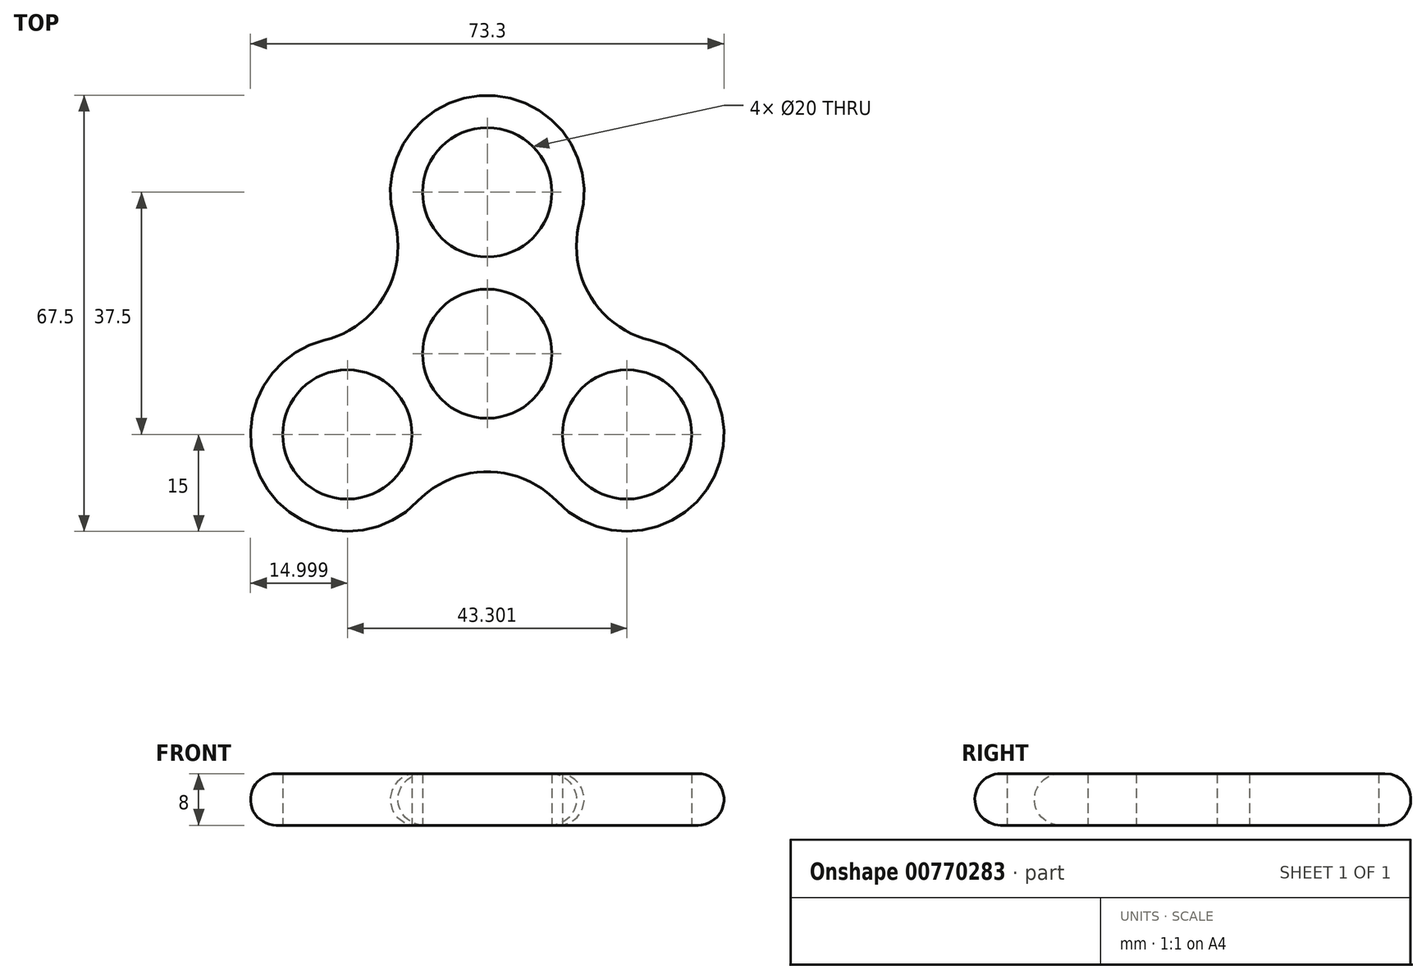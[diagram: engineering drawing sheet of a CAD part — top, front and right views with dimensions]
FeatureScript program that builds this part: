
annotation { "Feature Type Name" : "Feature", "Feature Type Description" : "" }
export const myFeature = defineFeature(function(context is Context, id is Id, definition is map)
    precondition{}
    {
        {
            assignVariable(context, id + "F0", {"name" : "bearing_thickness", "anyValue" : 8});
        }
        {
            var Q0;
            Q0=qCreatedBy(makeId("Top.planeOp"),FACE);
            var sketch = newSketch(context, id + "F1", { "sketchPlane" : qUnion([Q0])});
            skCircle(sketch, "E0", {"center": v(0, 25) * mm, "radius": 10 * mm});
            skArc(sketch, "E1", {"start": v(0, 40) * mm, "mid": v(12, 34) * mm, "end": v(14.4, 20.82) * mm});
            skArc(sketch, "E2", {"start": v(14.4, 20.82) * mm, "mid": v(15.82, 9.13) * mm, "end": v(25.23, 2.07) * mm});
            skArc(sketch, "E3.MirrorCS", {"start": v(0, 40) * mm, "mid": v(-12, 34) * mm, "end": v(-14.4, 20.82) * mm});
            skCircle(sketch, "E4.1.0", {"center": v(-21.65, -12.5) * mm, "radius": 10 * mm});
            skArc(sketch, "E4.1.1", {"start": v(-25.23, 2.07) * mm, "mid": v(-15.82, 9.13) * mm, "end": v(-14.4, 20.82) * mm});
            skArc(sketch, "E4.1.2", {"start": v(-34.64, -20) * mm, "mid": v(-23.45, -27.4) * mm, "end": v(-10.83, -22.88) * mm});
            skArc(sketch, "E4.1.3", {"start": v(-34.64, -20) * mm, "mid": v(-35.45, -6.62) * mm, "end": v(-25.23, 2.07) * mm});
            skCircle(sketch, "E4.2.0", {"center": v(21.65, -12.5) * mm, "radius": 10 * mm});
            skArc(sketch, "E4.2.1", {"start": v(10.83, -22.88) * mm, "mid": v(0, -18.27) * mm, "end": v(-10.83, -22.88) * mm});
            skArc(sketch, "E4.2.2", {"start": v(34.64, -20) * mm, "mid": v(35.45, -6.62) * mm, "end": v(25.23, 2.07) * mm});
            skArc(sketch, "E4.2.3", {"start": v(34.64, -20) * mm, "mid": v(23.45, -27.4) * mm, "end": v(10.83, -22.88) * mm});
            skPoint(sketch, "E4.center", {"position": v(0, 0) * mm});
            skCircle(sketch, "E5", {"center": v(0, 0) * mm, "radius": 10 * mm});
            skSolve(sketch);
        }
        {
            var Q0;
            Q0=makeQuery(id+"F1.imprint","IMPRINT",FACE,{"disambiguationData":[TD([[makeQuery(id+"F1.imprint","IMPRINT",EDGE,{"derivedFrom":sQuery(id+"F1.wireOp",EDGE,"E0")}),-1.0]])]});
            extrude(context, id + "F2", {"entities" : qUnion([Q0]), "depth" : getVariable(context, 'bearing_thickness') * mm, "offsetDistance" : 25 * mm});
        }
        {
            var Q0;
            Q0=makeQuery(id+"F2.opExtrude","CAP_EDGE",EDGE,{"disambiguationData":[OSD([sQuery(id+"F1.wireOp",EDGE,"E2")])],"isStart":false});
            var Q1;
            Q1=makeQuery(id+"F2.opExtrude","CAP_EDGE",EDGE,{"disambiguationData":[OSD([sQuery(id+"F1.wireOp",EDGE,"E2")])],"isStart":true});
            fillet(context, id + "F3", {"entities" : qUnion([Q0, Q1]), "radius" : getVariable(context, 'bearing_thickness') / 2 * mm, "tangentPropagation" : true, "allowEdgeOverflow" : false});
        }
    });
